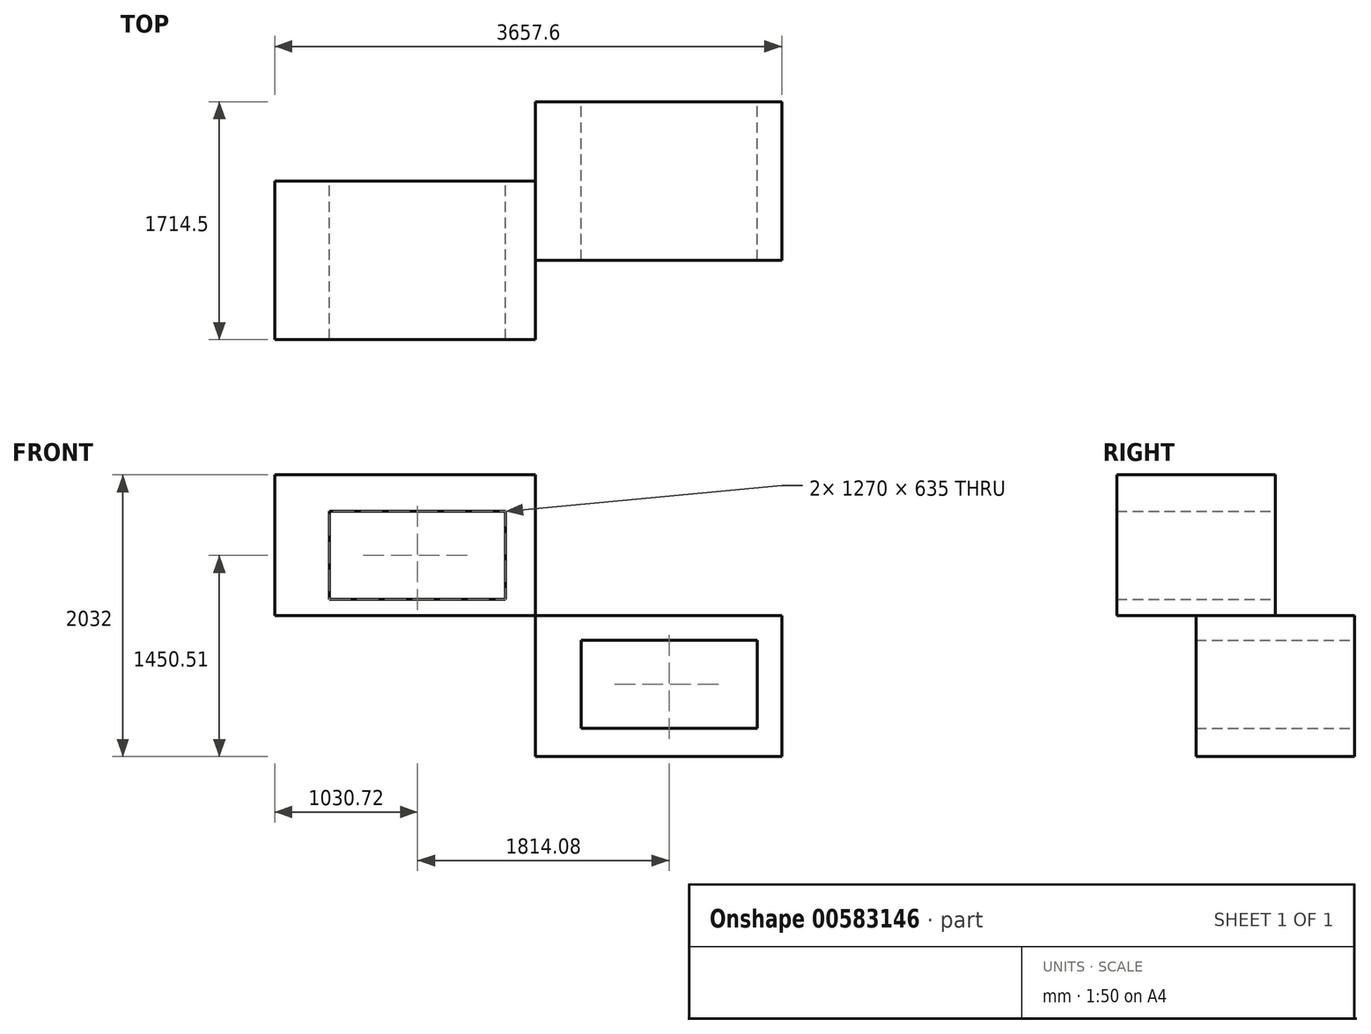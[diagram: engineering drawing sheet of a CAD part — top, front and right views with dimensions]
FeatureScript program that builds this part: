
annotation { "Feature Type Name" : "Feature", "Feature Type Description" : "" }
export const myFeature = defineFeature(function(context is Context, id is Id, definition is map)
    precondition{}
    {
        {
            var Q0;
            Q0=qCreatedBy(makeId("Front.planeOp"),FACE);
            var sketch = newSketch(context, id + "F0", { "sketchPlane" : qUnion([Q0])});
            skLineSegment(sketch, "E0.bottom", {"start": v(0, 0) * mm, "end": v(1778, 0) * mm});
            skLineSegment(sketch, "E0.top", {"start": v(0, -1016) * mm, "end": v(1778, -1016) * mm});
            skLineSegment(sketch, "E0.left", {"start": v(0, 0) * mm, "end": v(0, -1016) * mm});
            skLineSegment(sketch, "E0.right", {"start": v(1778, 0) * mm, "end": v(1778, -1016) * mm});
            skLineSegment(sketch, "E1.bottom", {"start": v(330.2, -177.8) * mm, "end": v(1600.2, -177.8) * mm});
            skLineSegment(sketch, "E1.top", {"start": v(330.2, -812.8) * mm, "end": v(1600.2, -812.8) * mm});
            skLineSegment(sketch, "E1.left", {"start": v(330.2, -177.8) * mm, "end": v(330.2, -812.8) * mm});
            skLineSegment(sketch, "E1.right", {"start": v(1600.2, -177.8) * mm, "end": v(1600.2, -812.8) * mm});
            skSolve(sketch);
        }
        {
            var Q0;
            Q0=makeQuery(id+"F0.imprint","IMPRINT",FACE,{"disambiguationData":[TD([[makeQuery(id+"F0.imprint","IMPRINT",EDGE,{"derivedFrom":sQuery(id+"F0.wireOp",EDGE,"E0.bottom")}),-1.0]])]});
            extrude(context, id + "F1", {"entities" : qUnion([Q0]), "depth" : 1143 * mm, "offsetDistance" : 25.4 * mm});
        }
        {
            var Q0;
            Q0=makeQuery(id+"F1.opExtrude","CAP_FACE",FACE,{"disambiguationData":[OSD([sQuery(id+"F0.wireOp",EDGE,"E0.bottom"),sQuery(id+"F0.wireOp",EDGE,"E0.top"),sQuery(id+"F0.wireOp",EDGE,"E0.left"),sQuery(id+"F0.wireOp",EDGE,"E0.right"),sQuery(id+"F0.wireOp",EDGE,"E1.bottom"),sQuery(id+"F0.wireOp",EDGE,"E1.top"),sQuery(id+"F0.wireOp",EDGE,"E1.left"),sQuery(id+"F0.wireOp",EDGE,"E1.right")])],"isStart":false});
            var sketch = newSketch(context, id + "F2", { "sketchPlane" : qUnion([Q0])});
            skLineSegment(sketch, "E2.bottom", {"start": v(0, 0) * mm, "end": v(-1879.6, 0) * mm});
            skLineSegment(sketch, "E2.top", {"start": v(0, 1016) * mm, "end": v(-1879.6, 1016) * mm});
            skLineSegment(sketch, "E2.left", {"start": v(0, 0) * mm, "end": v(0, 1016) * mm});
            skLineSegment(sketch, "E2.right", {"start": v(-1879.6, 0) * mm, "end": v(-1879.6, 1016) * mm});
            skLineSegment(sketch, "E3.bottom", {"start": v(-1483.88, 752.01) * mm, "end": v(-213.88, 752.01) * mm});
            skLineSegment(sketch, "E3.top", {"start": v(-1483.88, 117.01) * mm, "end": v(-213.88, 117.01) * mm});
            skLineSegment(sketch, "E3.left", {"start": v(-1483.88, 752.01) * mm, "end": v(-1483.88, 117.01) * mm});
            skLineSegment(sketch, "E3.right", {"start": v(-213.88, 752.01) * mm, "end": v(-213.88, 117.01) * mm});
            skSolve(sketch);
        }
        {
            var Q0;
            Q0 = qSketchRegion(id + "F2", true);
            extrude(context, id + "F3", {"entities" : qUnion([Q0]), "endBound" : BoundingType.SYMMETRIC, "depth" : 1143 * mm, "offsetDistance" : 25.4 * mm});
        }
    });
